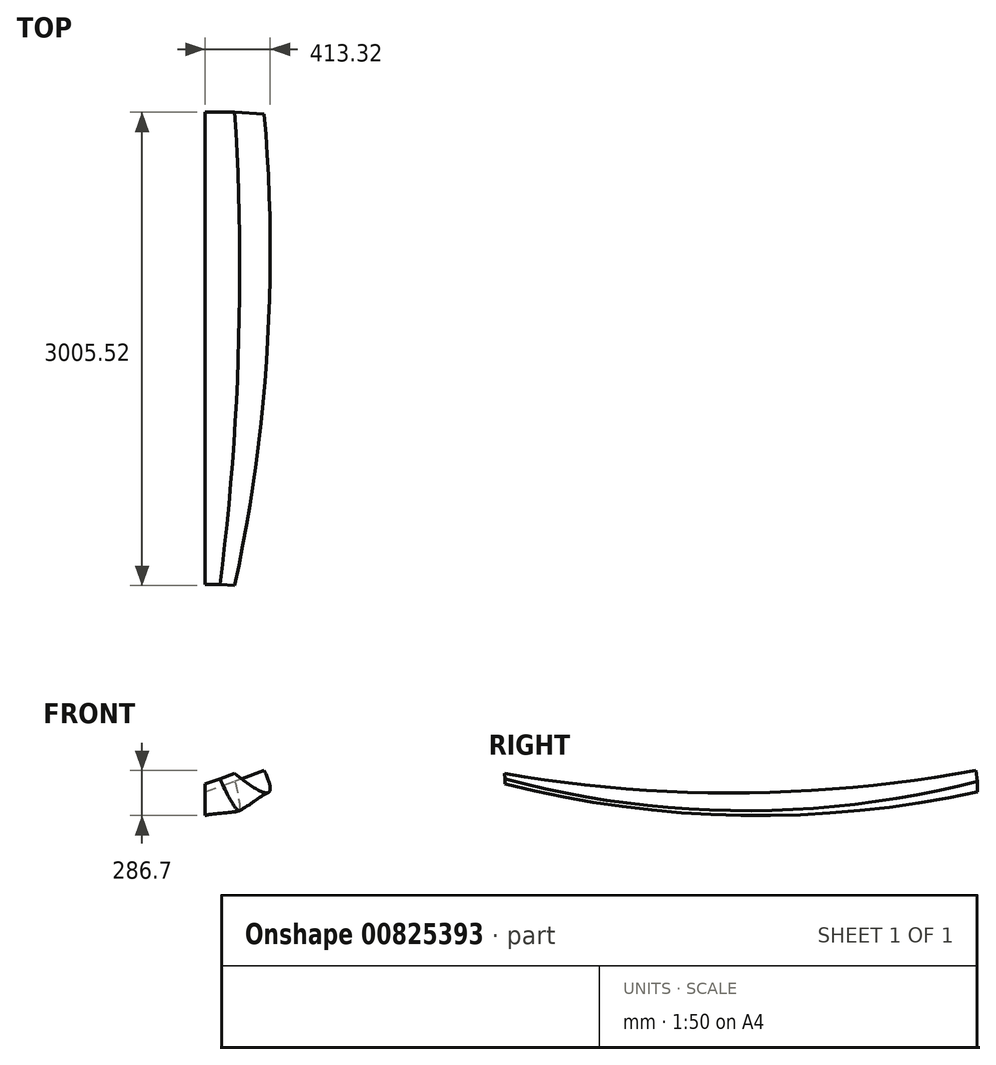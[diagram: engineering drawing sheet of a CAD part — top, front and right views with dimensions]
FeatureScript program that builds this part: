
annotation { "Feature Type Name" : "Feature", "Feature Type Description" : "" }
export const myFeature = defineFeature(function(context is Context, id is Id, definition is map)
    precondition{}
    {
        {
            var Q0;
            Q0=qCreatedBy(makeId("Right.planeOp"),FACE);
            var sketch = newSketch(context, id + "F0", { "sketchPlane" : qUnion([Q0])});
            skLineSegment(sketch, "E0", {"start": v(0, 0) * mm, "end": v(0, 150) * mm, "construction": true});
            skLineSegment(sketch, "E1", {"start": v(0, 0) * mm, "end": v(-3000, 0) * mm, "construction": true});
            skLineSegment(sketch, "E2", {"start": v(-3000, 0) * mm, "end": v(-3000, 200) * mm, "construction": true});
            skArc(sketch, "E3", {"start": v(-3000, 200) * mm, "mid": v(-1502.9, 0.9) * mm, "end": v(0, 150) * mm});
            skSolve(sketch);
        }
        {
            var Q0;
            Q0=qCreatedBy(makeId("Front.planeOp"),FACE);
            cPlane(context, id + "F1", {"entities" : qUnion([Q0]), "cplaneType" : CPlaneType.OFFSET, "offset" : 3000 * mm, "width" : 150 * mm, "height" : 150 * mm});
        }
        {
            var Q0;
            Q0=qCreatedBy(id+"F1.planeOp",FACE);
            var sketch = newSketch(context, id + "F2", { "sketchPlane" : qUnion([Q0])});
            skLineSegment(sketch, "E4", {"start": v(0, 200) * mm, "end": v(93.97, 234.2) * mm});
            skLineSegment(sketch, "E5", {"start": v(0, 200) * mm, "end": v(0, 552.03) * mm, "construction": true});
            skLineSegment(sketch, "E6", {"start": v(-4.37, 358.2) * mm, "end": v(46.98, 217.1) * mm});
            skLineSegment(sketch, "E7", {"start": v(93.97, 234.2) * mm, "end": v(29.7, 410.77) * mm});
            skSolve(sketch);
        }
        {
            var Q0;
            Q0=qCreatedBy(makeId("Front.planeOp"),FACE);
            var sketch = newSketch(context, id + "F3", { "sketchPlane" : qUnion([Q0])});
            skLineSegment(sketch, "E8", {"start": v(0, 150) * mm, "end": v(187.94, 218.4) * mm});
            skLineSegment(sketch, "E9", {"start": v(0, 0) * mm, "end": v(0, 345.43) * mm, "construction": true});
            skLineSegment(sketch, "E10", {"start": v(5.7, 426.7) * mm, "end": v(93.97, 184.2) * mm});
            skSolve(sketch);
        }
        {
            var Q0;
            Q0=sQuery(id+"F3.wireOp",VERTEX,"E8.end");
            var Q1;
            Q1=sQuery(id+"F0.wireOp",VERTEX,"E0.end");
            var Q2;
            Q2=sQuery(id+"F2.wireOp",VERTEX,"E4.end");
            cPlane(context, id + "F4", {"entities" : qUnion([Q0, Q1, Q2]), "cplaneType" : CPlaneType.THREE_POINT, "offset" : 25 * mm, "width" : 150 * mm, "height" : 150 * mm});
        }
        {
            var Q0;
            Q0=sQuery(id+"F3.wireOp",VERTEX,"E10.start");
            var Q1;
            Q1=sQuery(id+"F3.wireOp",VERTEX,"E10.end");
            var Q2;
            Q2=sQuery(id+"F2.wireOp",VERTEX,"E6.end");
            cPlane(context, id + "F5", {"entities" : qUnion([Q0, Q1, Q2]), "cplaneType" : CPlaneType.THREE_POINT, "offset" : 25 * mm, "width" : 150 * mm, "height" : 150 * mm});
        }
        {
            var Q0;
            Q0=qCreatedBy(id+"F5.planeOp",FACE);
            var sketch = newSketch(context, id + "F6", { "sketchPlane" : qUnion([Q0])});
            skLineSegment(sketch, "E11", {"start": v(1.66, 140.95) * mm, "end": v(-2998.52, 187.94) * mm, "construction": true});
            skLineSegment(sketch, "E12", {"start": v(-1198.34, 159.75) * mm, "end": v(-1198.34, -40.25) * mm, "construction": true});
            skArc(sketch, "E13", {"start": v(-2998.52, 187.94) * mm, "mid": v(-1501.7, -43.86) * mm, "end": v(1.66, 140.95) * mm});
            skSolve(sketch);
        }
        {
            var Q0;
            Q0=sQuery(id+"F2.wireOp",VERTEX,"E7.end");
            var Q1;
            Q1=sQuery(id+"F2.wireOp",VERTEX,"E4.end");
            var Q2;
            Q2=sQuery(id+"F3.wireOp",VERTEX,"E8.end");
            cPlane(context, id + "F7", {"entities" : qUnion([Q0, Q1, Q2]), "cplaneType" : CPlaneType.THREE_POINT, "offset" : 25 * mm, "width" : 150 * mm, "height" : 150 * mm});
        }
        {
            var Q0;
            Q0=qCreatedBy(id+"F7.planeOp",FACE);
            var sketch = newSketch(context, id + "F8", { "sketchPlane" : qUnion([Q0])});
            skLineSegment(sketch, "E14", {"start": v(-6.94, 140.95) * mm, "end": v(2994.2, 187.94) * mm, "construction": true});
            skLineSegment(sketch, "E15", {"start": v(1193.06, 159.74) * mm, "end": v(1201.48, -40.08) * mm, "construction": true});
            skArc(sketch, "E16", {"start": v(-6.94, 140.95) * mm, "mid": v(1496.88, -43.36) * mm, "end": v(2994.2, 187.94) * mm});
            skSolve(sketch);
        }
        {
            var Q0;
            Q0=sQuery(id+"F3.wireOp",EDGE,"E8");
            var Q1;
            Q1=sQuery(id+"F2.wireOp",EDGE,"E4");
            var Q2;
            Q2=sQuery(id+"F0.wireOp",EDGE,"E3");
            var Q3;
            Q3=sQuery(id+"F8.wireOp",EDGE,"E16");
            loft(context, id + "F9", {"bodyType" : ToolBodyType.SURFACE, "addGuides" : true, "wireProfilesArray" : [{ "wireProfileEntities" : qUnion([Q0]) }, { "wireProfileEntities" : qUnion([Q1]) }], "guidesArray" : [{ "guideEntities" : qUnion([Q2]), "guideDerivativeType" : LoftGuideDerivativeType.DEFAULT, "guideDerivativeMagnitude" : 1 }, { "guideEntities" : qUnion([Q3]), "guideDerivativeType" : LoftGuideDerivativeType.DEFAULT, "guideDerivativeMagnitude" : 1 }]});
        }
        {
            var Q0;
            Q0=makeQuery(id+"F9.opLoft","SWEPT_BODY",BODY,{"disambiguationData":[OSD([sQuery(id+"F0.wireOp",EDGE,"E3"),sQuery(id+"F2.wireOp",EDGE,"E4"),sQuery(id+"F3.wireOp",EDGE,"E8"),sQuery(id+"F8.wireOp",EDGE,"E16")])]});
            var Q1;
            Q1=qCreatedBy(id+"F7.planeOp",FACE);
            mirror(context, id + "F10", {"entities" : qUnion([Q0]), "mirrorPlane" : qUnion([Q1])});
        }
    });
